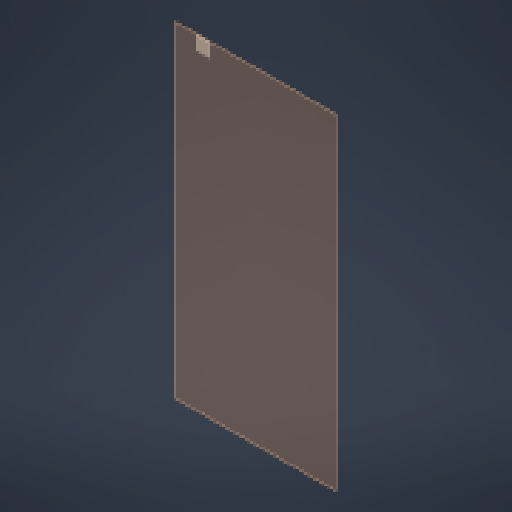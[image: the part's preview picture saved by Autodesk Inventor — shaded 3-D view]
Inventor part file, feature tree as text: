
AUTODESK INVENTOR PART (.ipt)
format: ipt  version: 2024 (Build 280153000, 153)  size: 124,928 bytes
history: native  units: mm
features: other x5, plane x1, extrude x1, sketch x1
ambient origin geometry x8: Origin, YZ Plane, XZ Plane, XY Plane, X Axis, Y Axis, Z Axis, Center Point
bodies: Body1 (feature_tree)
feature tree (8):
  other  "Sólido1"
  plane  "Plano de trabajo1"
  extrude  "Extrusión1"  Depth=30.0mm
  sketch  "Boceto1"  dims[d0=120.0mm d1=30.0mm d2=30.0mm d3=30.0mm d4=2.0mm d5=0.0mm]
  other  "<userpath>\Downloads\Piezas CMR\Marco_APM_002\Marco_apm_002-2.iam"
  other  "Marco_apm_002-2.iam"
  other  "Marco_Conveyor_Aereo:1"
  other  "Marco:1"
